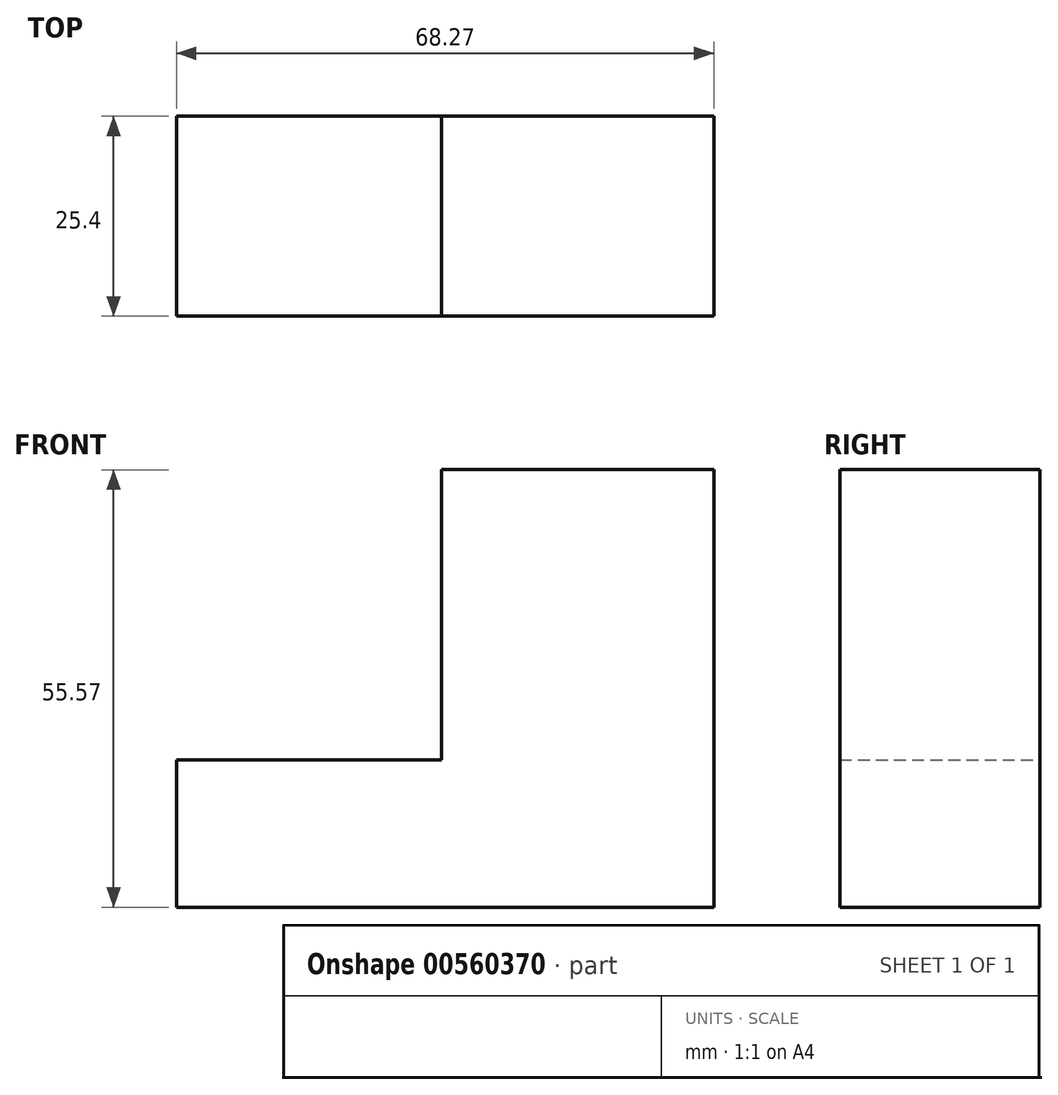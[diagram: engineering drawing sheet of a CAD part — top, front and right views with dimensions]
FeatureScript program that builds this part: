
annotation { "Feature Type Name" : "Feature", "Feature Type Description" : "" }
export const myFeature = defineFeature(function(context is Context, id is Id, definition is map)
    precondition{}
    {
        {
            var Q0;
            Q0=qCreatedBy(makeId("Front.planeOp"),FACE);
            var sketch = newSketch(context, id + "F0", { "sketchPlane" : qUnion([Q0])});
            skLineSegment(sketch, "E0", {"start": v(0, 0) * mm, "end": v(55.57, 0) * mm});
            skLineSegment(sketch, "E1", {"start": v(55.57, 0) * mm, "end": v(55.57, 55.57) * mm});
            skLineSegment(sketch, "E2", {"start": v(55.57, 55.57) * mm, "end": v(33.7, 55.57) * mm});
            skLineSegment(sketch, "E3", {"start": v(33.7, 55.57) * mm, "end": v(33.7, 18.72) * mm});
            skLineSegment(sketch, "E4", {"start": v(33.7, 18.72) * mm, "end": v(0, 18.72) * mm});
            skLineSegment(sketch, "E5", {"start": v(0, 18.72) * mm, "end": v(0, 0) * mm});
            skSolve(sketch);
        }
        {
            var Q0;
            Q0=makeQuery(id+"F0.imprint","IMPRINT",FACE,{"disambiguationData":[TD([[makeQuery(id+"F0.imprint","IMPRINT",EDGE,{"derivedFrom":sQuery(id+"F0.wireOp",EDGE,"E0")}),1.0]])]});
            extrude(context, id + "F1", {"entities" : qUnion([Q0]), "depth" : 25.4 * mm, "offsetDistance" : 25.4 * mm});
        }
        {
            var Q0;
            Q0=makeQuery(id+"F1.opExtrude","SWEPT_FACE",FACE,{"disambiguationData":[OSD([sQuery(id+"F0.wireOp",EDGE,"E1")])]});
            extrude(context, id + "F2", {"entities" : qUnion([Q0]), "operationType" : NewBodyOperationType.ADD, "endBound" : BoundingType.SYMMETRIC, "depth" : 25.4 * mm, "offsetDistance" : 25.4 * mm});
        }
    });
